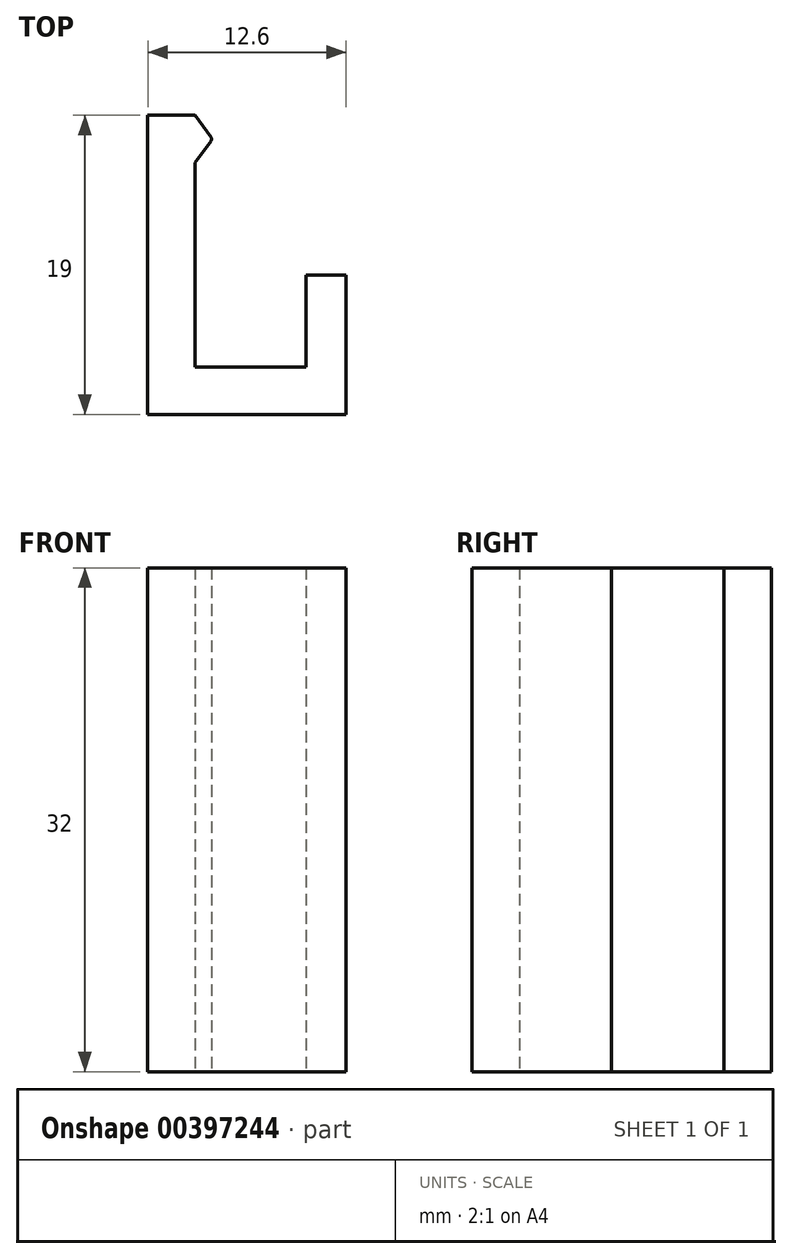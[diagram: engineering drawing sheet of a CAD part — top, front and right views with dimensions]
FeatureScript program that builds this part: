
annotation { "Feature Type Name" : "Feature", "Feature Type Description" : "" }
export const myFeature = defineFeature(function(context is Context, id is Id, definition is map)
    precondition{}
    {
        {
            var Q0;
            Q0=qCreatedBy(makeId("Top.planeOp"),FACE);
            var sketch = newSketch(context, id + "F0", { "sketchPlane" : qUnion([Q0])});
            skLineSegment(sketch, "E0", {"start": v(-32.18, 6.68) * mm, "end": v(-19.58, 6.68) * mm});
            skLineSegment(sketch, "E1", {"start": v(-19.58, 6.68) * mm, "end": v(-19.58, 15.53) * mm});
            skLineSegment(sketch, "E2.0", {"start": v(-22.13, 9.68) * mm, "end": v(-22.13, 15.53) * mm});
            skLineSegment(sketch, "E2.1", {"start": v(-29.18, 9.68) * mm, "end": v(-22.13, 9.68) * mm});
            skLineSegment(sketch, "E3", {"start": v(-22.13, 15.53) * mm, "end": v(-19.58, 15.53) * mm});
            skLineSegment(sketch, "E4", {"start": v(-32.18, 6.68) * mm, "end": v(-32.18, 25.68) * mm});
            skLineSegment(sketch, "E5", {"start": v(-29.18, 9.68) * mm, "end": v(-29.18, 22.68) * mm});
            skLineSegment(sketch, "E6", {"start": v(-29.18, 25.68) * mm, "end": v(-28.18, 24.28) * mm});
            skLineSegment(sketch, "E7", {"start": v(-32.18, 25.68) * mm, "end": v(-29.18, 25.68) * mm});
            skLineSegment(sketch, "E8", {"start": v(-28.18, 24.05) * mm, "end": v(-29.18, 22.68) * mm});
            skPoint(sketch, "E9.visualSharp", {"position": v(-28.1, 24.17) * mm});
            skArc(sketch, "E9.filletArc", {"start": v(-28.18, 24.05) * mm, "mid": v(-28.14, 24.17) * mm, "end": v(-28.18, 24.28) * mm});
            skLineSegment(sketch, "E10", {"start": v(-28.1, 25.95) * mm, "end": v(-28.1, 21.75) * mm, "construction": true});
            skSolve(sketch);
        }
        {
            var Q0;
            Q0=makeQuery(id+"F0.imprint","IMPRINT",FACE,{"disambiguationData":[TD([[makeQuery(id+"F0.imprint","IMPRINT",EDGE,{"derivedFrom":sQuery(id+"F0.wireOp",EDGE,"E0")}),1.0]])]});
            extrude(context, id + "F1", {"entities" : qUnion([Q0]), "depth" : 32 * mm});
        }
    });
